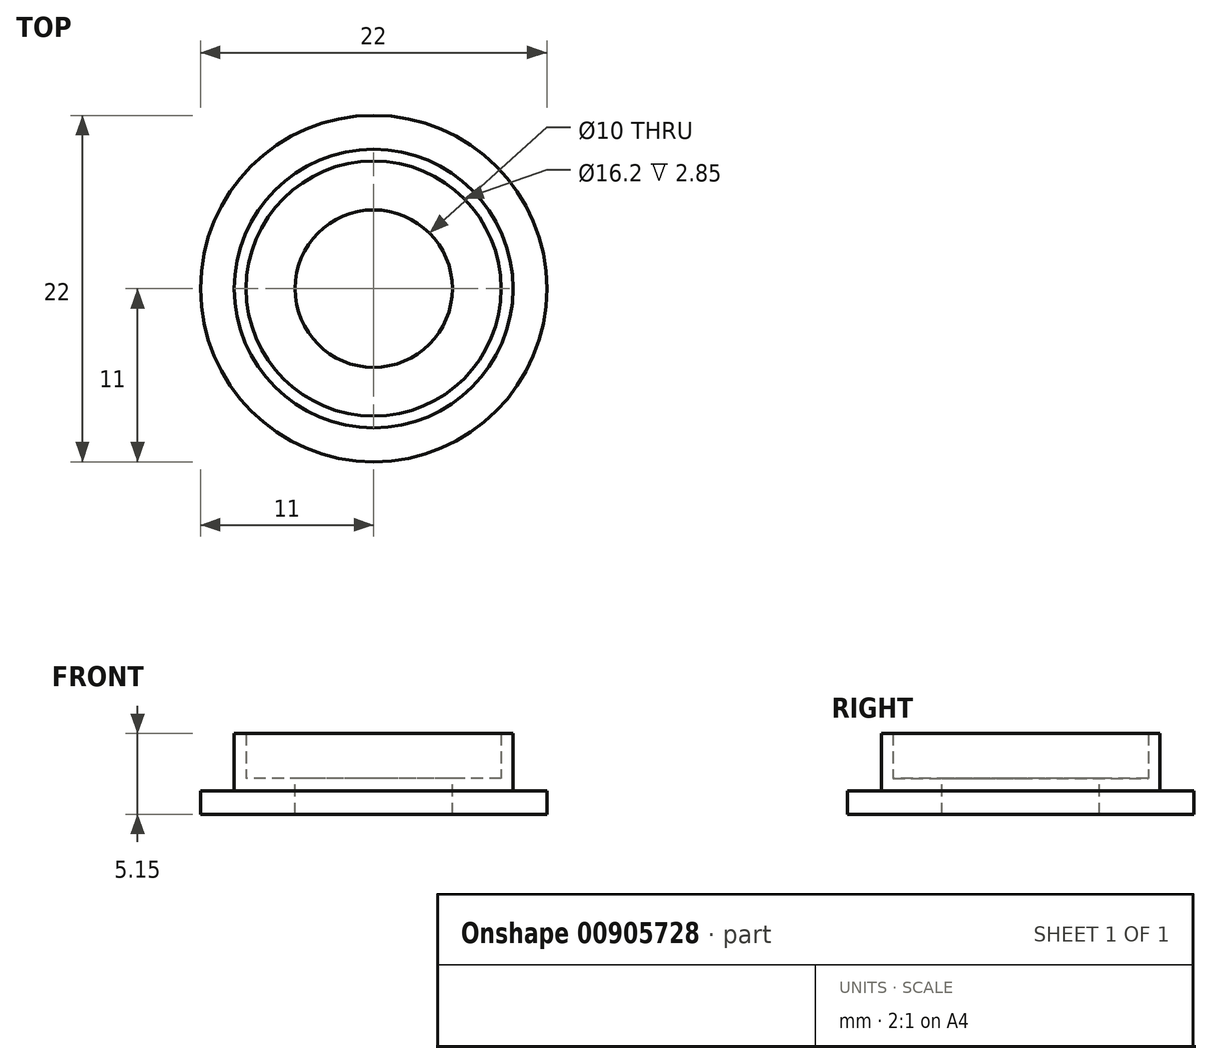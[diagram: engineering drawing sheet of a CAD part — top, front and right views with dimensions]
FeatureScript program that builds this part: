
annotation { "Feature Type Name" : "Feature", "Feature Type Description" : "" }
export const myFeature = defineFeature(function(context is Context, id is Id, definition is map)
    precondition{}
    {
        {
            var Q0;
            Q0=qCreatedBy(makeId("Top.planeOp"),FACE);
            var sketch = newSketch(context, id + "F0", { "sketchPlane" : qUnion([Q0])});
            skCircle(sketch, "E0", {"center": v(0, 0) * mm, "radius": 11 * mm});
            skCircle(sketch, "E1", {"center": v(0, 0) * mm, "radius": 8.85 * mm});
            skCircle(sketch, "E2", {"center": v(0, 0) * mm, "radius": 8.1 * mm});
            skCircle(sketch, "E3", {"center": v(0, 0) * mm, "radius": 5 * mm});
            skSolve(sketch);
        }
        {
            var Q0;
            Q0=makeQuery(id+"F0.imprint","IMPRINT",FACE,{"disambiguationData":[TD([[makeQuery(id+"F0.imprint","IMPRINT",EDGE,{"derivedFrom":sQuery(id+"F0.wireOp",EDGE,"E0")}),1.0]])]});
            var Q1;
            Q1=makeQuery(id+"F0.imprint","IMPRINT",FACE,{"disambiguationData":[TD([[makeQuery(id+"F0.imprint","IMPRINT",EDGE,{"derivedFrom":sQuery(id+"F0.wireOp",EDGE,"E2")}),1.0]])]});
            var Q2;
            Q2=makeQuery(id+"F0.imprint","IMPRINT",FACE,{"disambiguationData":[TD([[makeQuery(id+"F0.imprint","IMPRINT",EDGE,{"derivedFrom":sQuery(id+"F0.wireOp",EDGE,"E1")}),1.0]])]});
            extrude(context, id + "F1", {"entities" : qUnion([Q0, Q1, Q2]), "oppositeDirection" : true, "depth" : 1.5 * mm, "offsetDistance" : 25 * mm});
        }
        {
            var Q0;
            Q0=makeQuery(id+"F0.imprint","IMPRINT",FACE,{"disambiguationData":[TD([[makeQuery(id+"F0.imprint","IMPRINT",EDGE,{"derivedFrom":sQuery(id+"F0.wireOp",EDGE,"E1")}),1.0]])]});
            extrude(context, id + "F2", {"entities" : qUnion([Q0]), "operationType" : NewBodyOperationType.ADD, "depth" : (5.3 / 2) * mm, "offsetDistance" : 25 * mm});
        }
        {
            var Q0;
            Q0=makeQuery(id+"F2.opExtrude","CAP_FACE",FACE,{"disambiguationData":[OSD([sQuery(id+"F0.wireOp",EDGE,"E1"),sQuery(id+"F0.wireOp",EDGE,"E2")])],"isStart":false});
            extrude(context, id + "F3", {"entities" : qUnion([Q0]), "operationType" : NewBodyOperationType.ADD, "depth" : 1 * mm, "offsetDistance" : 25 * mm});
        }
        {
            var Q0;
            {var subQ0=sQuery(id+"F0.wireOp",EDGE,"E3");Q0=makeQuery(id+"F2.boolean.opBoolean","SPLIT",FACE,{"disambiguationData":[TD([makeQuery(id+"F1.opExtrude","SWEPT_FACE",FACE,{"disambiguationData":[OSD([subQ0])]})])],"derivedFrom":makeQuery(id+"F1.opExtrude","CAP_FACE",FACE,{"disambiguationData":[OSD([sQuery(id+"F0.wireOp",EDGE,"E0"),subQ0])],"isStart":true})});}
            extrude(context, id + "F4", {"entities" : qUnion([Q0]), "operationType" : NewBodyOperationType.ADD, "depth" : 0.8 * mm, "offsetDistance" : 25 * mm});
        }
    });
